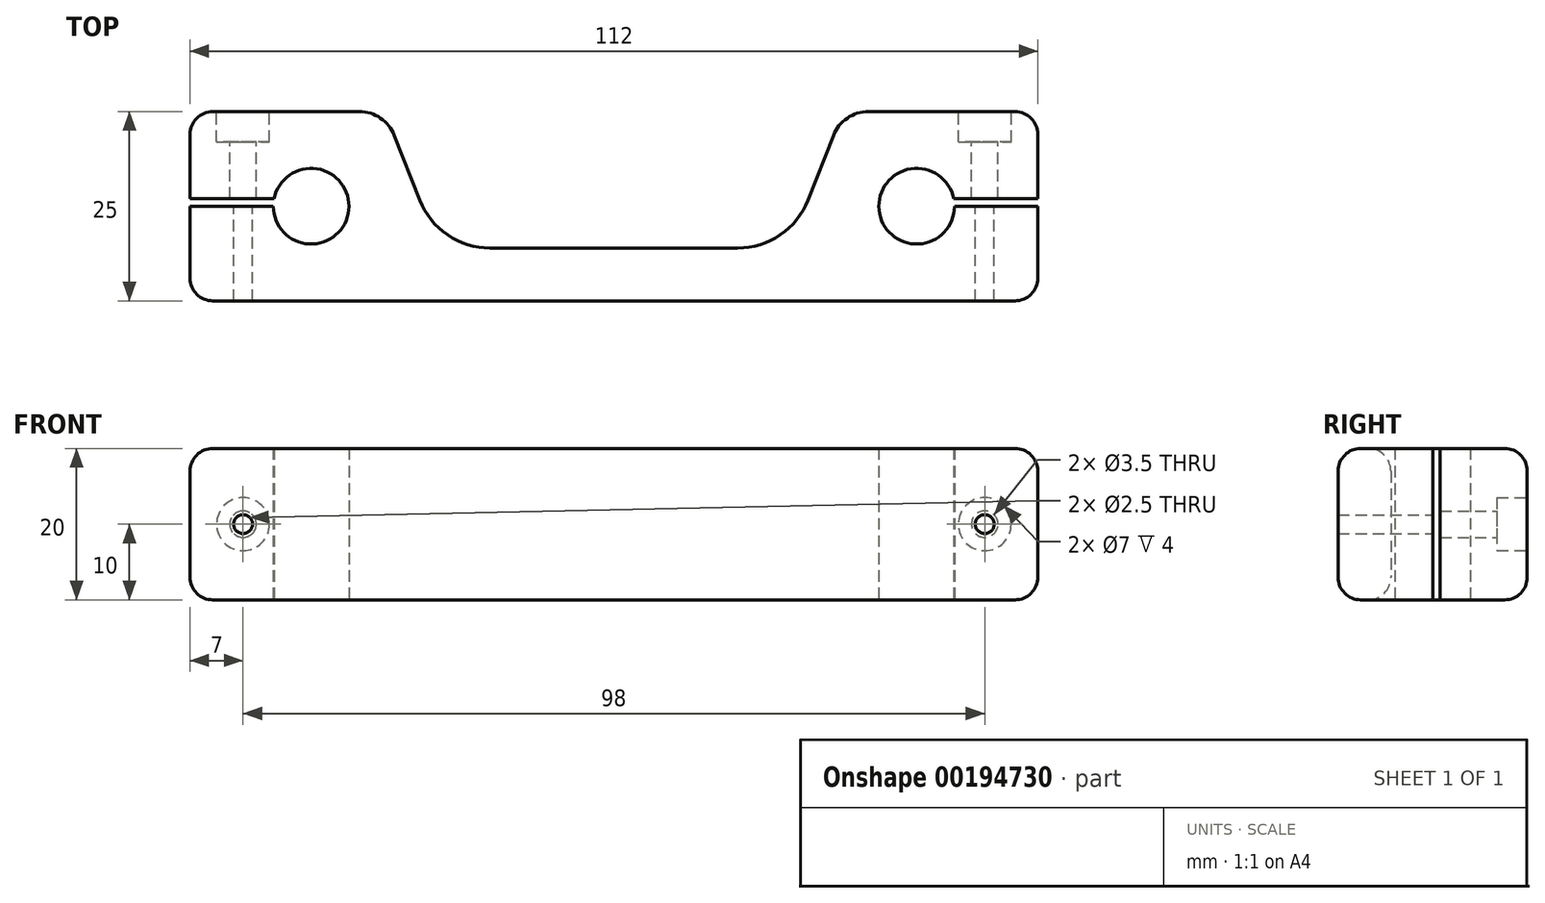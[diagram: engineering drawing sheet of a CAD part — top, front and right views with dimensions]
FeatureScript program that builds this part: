
annotation { "Feature Type Name" : "Feature", "Feature Type Description" : "" }
export const myFeature = defineFeature(function(context is Context, id is Id, definition is map)
    precondition{}
    {
        {
            var Q0;
            Q0=qCreatedBy(makeId("Top.planeOp"),FACE);
            var sketch = newSketch(context, id + "F0", { "sketchPlane" : qUnion([Q0])});
            skLineSegment(sketch, "E0", {"start": v(56, 0) * mm, "end": v(109, 0) * mm});
            skLineSegment(sketch, "E1", {"start": v(112, 3) * mm, "end": v(112, 12.5) * mm});
            skLineSegment(sketch, "E2", {"start": v(109, 25) * mm, "end": v(95.8, 25) * mm});
            skArc(sketch, "E3", {"start": v(100.9, 13.5) * mm, "mid": v(91.03, 12) * mm, "end": v(101, 12.5) * mm});
            skLineSegment(sketch, "E4", {"start": v(61.96, 6.98) * mm, "end": v(56, 6.98) * mm});
            skLineSegment(sketch, "E5", {"start": v(61.96, 6.98) * mm, "end": v(72.35, 6.98) * mm});
            skPoint(sketch, "E6.visualSharp", {"position": v(92, 25) * mm});
            skPoint(sketch, "E7.visualSharp", {"position": v(86.96, 6.98) * mm});
            skPoint(sketch, "E8.visualSharp", {"position": v(112, 25) * mm});
            skArc(sketch, "E8.filletArc", {"start": v(112, 22) * mm, "mid": v(111.12, 24.12) * mm, "end": v(109, 25) * mm});
            skPoint(sketch, "E9.visualSharp", {"position": v(112, 0) * mm});
            skArc(sketch, "E9.filletArc", {"start": v(109, 0) * mm, "mid": v(111.12, 0.88) * mm, "end": v(112, 3) * mm});
            skLineSegment(sketch, "E10", {"start": v(96, 12.5) * mm, "end": v(112, 12.5) * mm});
            skLineSegment(sketch, "E11.trimOffspring", {"start": v(112, 13.5) * mm, "end": v(112, 22) * mm});
            skLineSegment(sketch, "E12", {"start": v(96, 12.5) * mm, "end": v(96, 13.5) * mm});
            skLineSegment(sketch, "E13", {"start": v(96, 13.5) * mm, "end": v(112, 13.5) * mm});
            skLineSegment(sketch, "E14", {"start": v(89.65, 25) * mm, "end": v(92, 25) * mm});
            skLineSegment(sketch, "E15", {"start": v(92, 25) * mm, "end": v(89.65, 25) * mm});
            skLineSegment(sketch, "E16", {"start": v(81.66, 13.33) * mm, "end": v(85, 21.83) * mm});
            skLineSegment(sketch, "E17", {"start": v(92, 25) * mm, "end": v(95.8, 25) * mm});
            skPoint(sketch, "E18.orphan", {"position": v(79.37, 6.98) * mm});
            skPoint(sketch, "E19.visualSharp", {"position": v(86.24, 25) * mm});
            skArc(sketch, "E19.filletArc", {"start": v(89.65, 25) * mm, "mid": v(86.83, 24.13) * mm, "end": v(85, 21.83) * mm});
            skPoint(sketch, "E20.visualSharp", {"position": v(79.17, 6.98) * mm});
            skArc(sketch, "E20.filletArc", {"start": v(72.35, 6.98) * mm, "mid": v(77.98, 8.72) * mm, "end": v(81.66, 13.33) * mm});
            skLineSegment(sketch, "E21.MirrorCS", {"start": v(20, 25) * mm, "end": v(22.35, 25) * mm});
            skLineSegment(sketch, "E22.MirrorCS", {"start": v(16, 12.5) * mm, "end": v(16, 13.5) * mm});
            skLineSegment(sketch, "E23.MirrorCS", {"start": v(22.35, 25) * mm, "end": v(20, 25) * mm});
            skArc(sketch, "E24.MirrorCS", {"start": v(0, 22) * mm, "mid": v(0.88, 24.12) * mm, "end": v(3, 25) * mm});
            skArc(sketch, "E25.MirrorCS", {"start": v(3, 0) * mm, "mid": v(0.88, 0.88) * mm, "end": v(0, 3) * mm});
            skPoint(sketch, "E26.MirrorP", {"position": v(32.63, 6.98) * mm});
            skLineSegment(sketch, "E27.MirrorCS", {"start": v(50.04, 6.98) * mm, "end": v(39.65, 6.98) * mm});
            skArc(sketch, "E28.MirrorCS", {"start": v(22.35, 25) * mm, "mid": v(25.17, 24.13) * mm, "end": v(27, 21.83) * mm});
            skPoint(sketch, "E29.MirrorP", {"position": v(20, 25) * mm});
            skLineSegment(sketch, "E30.MirrorCS", {"start": v(20, 25) * mm, "end": v(16.2, 25) * mm});
            skLineSegment(sketch, "E31.MirrorCS", {"start": v(30.34, 13.33) * mm, "end": v(27, 21.83) * mm});
            skLineSegment(sketch, "E32.MirrorCS", {"start": v(16, 13.5) * mm, "end": v(0, 13.5) * mm});
            skArc(sketch, "E33.MirrorCS", {"start": v(11.1, 13.5) * mm, "mid": v(20.97, 12) * mm, "end": v(11, 12.5) * mm});
            skLineSegment(sketch, "E34.MirrorCS", {"start": v(50.04, 6.98) * mm, "end": v(56, 6.98) * mm});
            skPoint(sketch, "E35.MirrorP", {"position": v(32.83, 6.98) * mm});
            skPoint(sketch, "E36.MirrorP", {"position": v(0, 25) * mm});
            skArc(sketch, "E37.MirrorCS", {"start": v(39.65, 6.98) * mm, "mid": v(34.02, 8.72) * mm, "end": v(30.34, 13.33) * mm});
            skLineSegment(sketch, "E38.MirrorCS", {"start": v(56, 0) * mm, "end": v(3, 0) * mm});
            skPoint(sketch, "E39.MirrorP", {"position": v(25.76, 25) * mm});
            skLineSegment(sketch, "E40.MirrorCS", {"start": v(16, 12.5) * mm, "end": v(0, 12.5) * mm});
            skPoint(sketch, "E41.MirrorP", {"position": v(0, 0) * mm});
            skLineSegment(sketch, "E42.MirrorCS", {"start": v(3, 25) * mm, "end": v(16.2, 25) * mm});
            skLineSegment(sketch, "E43.MirrorCS", {"start": v(0, 13.5) * mm, "end": v(0, 22) * mm});
            skLineSegment(sketch, "E44.MirrorCS", {"start": v(0, 3) * mm, "end": v(0, 12.5) * mm});
            skPoint(sketch, "E45.MirrorP", {"position": v(25.04, 6.98) * mm});
            skSolve(sketch);
        }
        {
            var Q0;
            Q0=makeQuery(id+"F0.imprint","IMPRINT",FACE,{"disambiguationData":[TD([[makeQuery(id+"F0.imprint","IMPRINT",EDGE,{"derivedFrom":sQuery(id+"F0.wireOp",EDGE,"E0")}),1.0]])]});
            extrude(context, id + "F1", {"entities" : qUnion([Q0]), "depth" : 20 * mm});
        }
        {
            var Q0;
            Q0=makeQuery(id+"F1.opExtrude","CAP_EDGE",EDGE,{"disambiguationData":[OSD([sQuery(id+"F0.wireOp",EDGE,"E0")])],"isStart":false});
            var Q1;
            Q1=makeQuery(id+"F1.opExtrude","CAP_EDGE",EDGE,{"disambiguationData":[OSD([sQuery(id+"F0.wireOp",EDGE,"85002565-1ed2-43ad-ab00-a444c3a869ad.trimOffspring")])],"isStart":false});
            var Q2;
            Q2=makeQuery(id+"F1.opExtrude","CAP_EDGE",EDGE,{"disambiguationData":[OSD([sQuery(id+"F0.wireOp",EDGE,"E2")])],"isStart":false});
            var Q3;
            Q3=makeQuery(id+"F1.opExtrude","CAP_EDGE",EDGE,{"disambiguationData":[OSD([sQuery(id+"F0.wireOp",EDGE,"E0")])],"isStart":true});
            var Q4;
            Q4=makeQuery(id+"F1.opExtrude","CAP_EDGE",EDGE,{"disambiguationData":[OSD([sQuery(id+"F0.wireOp",EDGE,"85002565-1ed2-43ad-ab00-a444c3a869ad.trimOffspring")])],"isStart":true});
            var Q5;
            Q5=makeQuery(id+"F1.opExtrude","CAP_EDGE",EDGE,{"disambiguationData":[OSD([sQuery(id+"F0.wireOp",EDGE,"E2")])],"isStart":true});
            fillet(context, id + "F2", {"entities" : qUnion([Q0, Q1, Q2, Q3, Q4, Q5]), "radius" : 3 * mm, "tangentPropagation" : true, "allowEdgeOverflow" : false});
        }
        {
            var Q0;
            Q0=makeQuery(id+"F1.opExtrude","SWEPT_FACE",FACE,{"disambiguationData":[OSD([sQuery(id+"F0.wireOp",EDGE,"E23.MirrorCS"),sQuery(id+"F0.wireOp",EDGE,"E30.MirrorCS"),sQuery(id+"F0.wireOp",EDGE,"E42.MirrorCS")])]});
            var sketch = newSketch(context, id + "F3", { "sketchPlane" : qUnion([Q0])});
            skLineSegment(sketch, "E46", {"start": v(-3, 17) * mm, "end": v(-7, 17) * mm});
            skCircle(sketch, "E47", {"center": v(-7, 10) * mm, "radius": 1.25 * mm});
            skCircle(sketch, "E48", {"center": v(-7, 10) * mm, "radius": 1.75 * mm});
            skCircle(sketch, "E49", {"center": v(-7, 10) * mm, "radius": 3.5 * mm});
            skSolve(sketch);
        }
        {
            var Q0;
            Q0=makeQuery(id+"F3.imprint","IMPRINT",FACE,{"disambiguationData":[TD([[makeQuery(id+"F3.imprint","IMPRINT",EDGE,{"derivedFrom":sQuery(id+"F3.wireOp",EDGE,"E47")}),1.0]])]});
            extrude(context, id + "F4", {"entities" : qUnion([Q0]), "operationType" : NewBodyOperationType.REMOVE, "oppositeDirection" : true, "depth" : 30 * mm});
        }
        {
            var Q0;
            Q0=makeQuery(id+"F3.imprint","IMPRINT",FACE,{"disambiguationData":[TD([[makeQuery(id+"F3.imprint","IMPRINT",EDGE,{"derivedFrom":sQuery(id+"F3.wireOp",EDGE,"E47")}),-1.0]])]});
            extrude(context, id + "F5", {"entities" : qUnion([Q0]), "operationType" : NewBodyOperationType.REMOVE, "oppositeDirection" : true, "depth" : 12 * mm});
        }
        {
            var Q0;
            Q0=makeQuery(id+"F3.imprint","IMPRINT",FACE,{"disambiguationData":[TD([[makeQuery(id+"F3.imprint","IMPRINT",EDGE,{"derivedFrom":sQuery(id+"F3.wireOp",EDGE,"E47")}),1.0]])]});
            var Q1;
            Q1=makeQuery(id+"F3.imprint","IMPRINT",FACE,{"disambiguationData":[TD([[makeQuery(id+"F3.imprint","IMPRINT",EDGE,{"derivedFrom":sQuery(id+"F3.wireOp",EDGE,"E47")}),-1.0]])]});
            var Q2;
            Q2=makeQuery(id+"F3.imprint","IMPRINT",FACE,{"disambiguationData":[TD([[makeQuery(id+"F3.imprint","IMPRINT",EDGE,{"derivedFrom":sQuery(id+"F3.wireOp",EDGE,"E48")}),-1.0]])]});
            extrude(context, id + "F6", {"entities" : qUnion([Q0, Q1, Q2]), "operationType" : NewBodyOperationType.REMOVE, "oppositeDirection" : true, "depth" : 4 * mm});
        }
        {
            var Q0;
            Q0=makeQuery(id+"F1.opExtrude","SWEPT_FACE",FACE,{"disambiguationData":[OSD([sQuery(id+"F0.wireOp",EDGE,"E2"),sQuery(id+"F0.wireOp",EDGE,"E15"),sQuery(id+"F0.wireOp",EDGE,"E17")])]});
            var sketch = newSketch(context, id + "F7", { "sketchPlane" : qUnion([Q0])});
            skLineSegment(sketch, "E50", {"start": v(-109, 17) * mm, "end": v(-105, 17) * mm});
            skCircle(sketch, "E51", {"center": v(-105, 10) * mm, "radius": 1.25 * mm});
            skCircle(sketch, "E52", {"center": v(-105, 10) * mm, "radius": 1.75 * mm});
            skCircle(sketch, "E53", {"center": v(-105, 10) * mm, "radius": 3.5 * mm});
            skSolve(sketch);
        }
        {
            var Q0;
            Q0=makeQuery(id+"F7.imprint","IMPRINT",FACE,{"disambiguationData":[TD([[makeQuery(id+"F7.imprint","IMPRINT",EDGE,{"derivedFrom":sQuery(id+"F7.wireOp",EDGE,"E51")}),1.0]])]});
            extrude(context, id + "F8", {"entities" : qUnion([Q0]), "operationType" : NewBodyOperationType.REMOVE, "oppositeDirection" : true, "depth" : 30 * mm});
        }
        {
            var Q0;
            Q0=makeQuery(id+"F7.imprint","IMPRINT",FACE,{"disambiguationData":[TD([[makeQuery(id+"F7.imprint","IMPRINT",EDGE,{"derivedFrom":sQuery(id+"F7.wireOp",EDGE,"E51")}),-1.0]])]});
            extrude(context, id + "F9", {"entities" : qUnion([Q0]), "operationType" : NewBodyOperationType.REMOVE, "oppositeDirection" : true, "depth" : 12 * mm});
        }
        {
            var Q0;
            Q0=makeQuery(id+"F7.imprint","IMPRINT",FACE,{"disambiguationData":[TD([[makeQuery(id+"F7.imprint","IMPRINT",EDGE,{"derivedFrom":sQuery(id+"F7.wireOp",EDGE,"E52")}),-1.0]])]});
            extrude(context, id + "F10", {"entities" : qUnion([Q0]), "operationType" : NewBodyOperationType.REMOVE, "oppositeDirection" : true, "depth" : 4 * mm});
        }
    });
